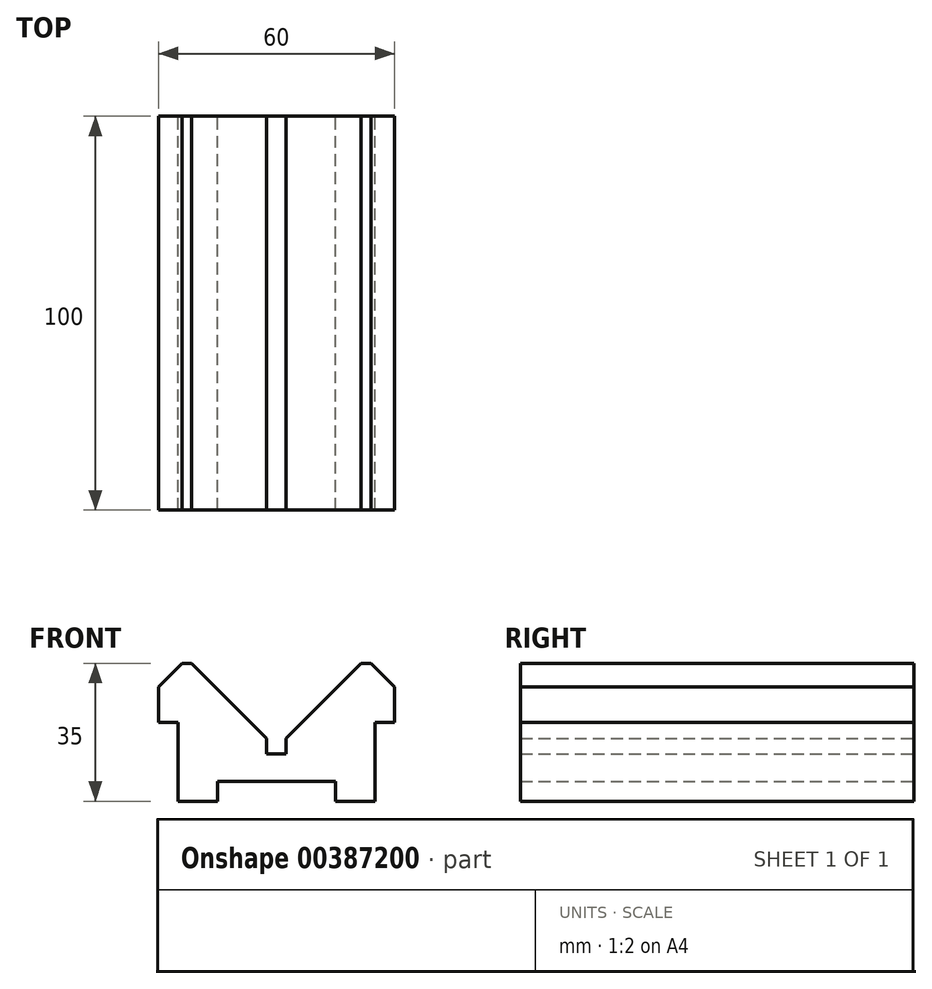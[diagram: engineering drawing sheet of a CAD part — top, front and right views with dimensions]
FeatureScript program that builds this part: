
annotation { "Feature Type Name" : "Feature", "Feature Type Description" : "" }
export const myFeature = defineFeature(function(context is Context, id is Id, definition is map)
    precondition{}
    {
        {
            var Q0;
            Q0=qCreatedBy(makeId("Front.planeOp"),FACE);
            var sketch = newSketch(context, id + "F0", { "sketchPlane" : qUnion([Q0])});
            skLineSegment(sketch, "E0.left", {"start": v(-30, 11.5) * mm, "end": v(-30, 2.5) * mm});
            skLineSegment(sketch, "E0.right", {"start": v(30, 11.5) * mm, "end": v(30, 2.5) * mm});
            skLineSegment(sketch, "E1.top", {"start": v(-30, 2.5) * mm, "end": v(-25, 2.5) * mm});
            skLineSegment(sketch, "E1.right", {"start": v(-25, -17.5) * mm, "end": v(-25, 2.5) * mm});
            skLineSegment(sketch, "E2.top", {"start": v(30, 2.5) * mm, "end": v(25, 2.5) * mm});
            skLineSegment(sketch, "E2.right", {"start": v(25, -17.5) * mm, "end": v(25, 2.5) * mm});
            skLineSegment(sketch, "E3", {"start": v(30, 11.5) * mm, "end": v(24, 17.5) * mm});
            skLineSegment(sketch, "E4", {"start": v(-30, 11.5) * mm, "end": v(-24, 17.5) * mm});
            skLineSegment(sketch, "E5.bottom", {"start": v(-15, -12.5) * mm, "end": v(15, -12.5) * mm});
            skLineSegment(sketch, "E5.left", {"start": v(-15, -12.5) * mm, "end": v(-15, -17.5) * mm});
            skLineSegment(sketch, "E5.right", {"start": v(15, -12.5) * mm, "end": v(15, -17.5) * mm});
            skLineSegment(sketch, "E6.trimOffspring", {"start": v(15, -17.5) * mm, "end": v(25, -17.5) * mm});
            skLineSegment(sketch, "E7", {"start": v(-25, -17.5) * mm, "end": v(-15, -17.5) * mm});
            skLineSegment(sketch, "E8.bottom", {"start": v(2.5, -5.5) * mm, "end": v(-2.5, -5.5) * mm});
            skLineSegment(sketch, "E8.left", {"start": v(2.5, -5.5) * mm, "end": v(2.5, -1.5) * mm});
            skLineSegment(sketch, "E8.right", {"start": v(-2.5, -5.5) * mm, "end": v(-2.5, -1.5) * mm});
            skLineSegment(sketch, "E9", {"start": v(-24, 17.5) * mm, "end": v(-21.5, 17.5) * mm});
            skLineSegment(sketch, "E10", {"start": v(21.5, 17.5) * mm, "end": v(24, 17.5) * mm});
            skPoint(sketch, "E11.orphan", {"position": v(21.5, 17.5) * mm});
            skLineSegment(sketch, "E12", {"start": v(2.5, -1.5) * mm, "end": v(21.5, 17.5) * mm});
            skLineSegment(sketch, "E13", {"start": v(-21.5, 17.5) * mm, "end": v(-2.5, -1.5) * mm});
            skSolve(sketch);
        }
        {
            var Q0;
            Q0 = qSketchRegion(id + "F0", true);
            extrude(context, id + "F1", {"entities" : qUnion([Q0]), "depth" : 100 * mm});
        }
    });
